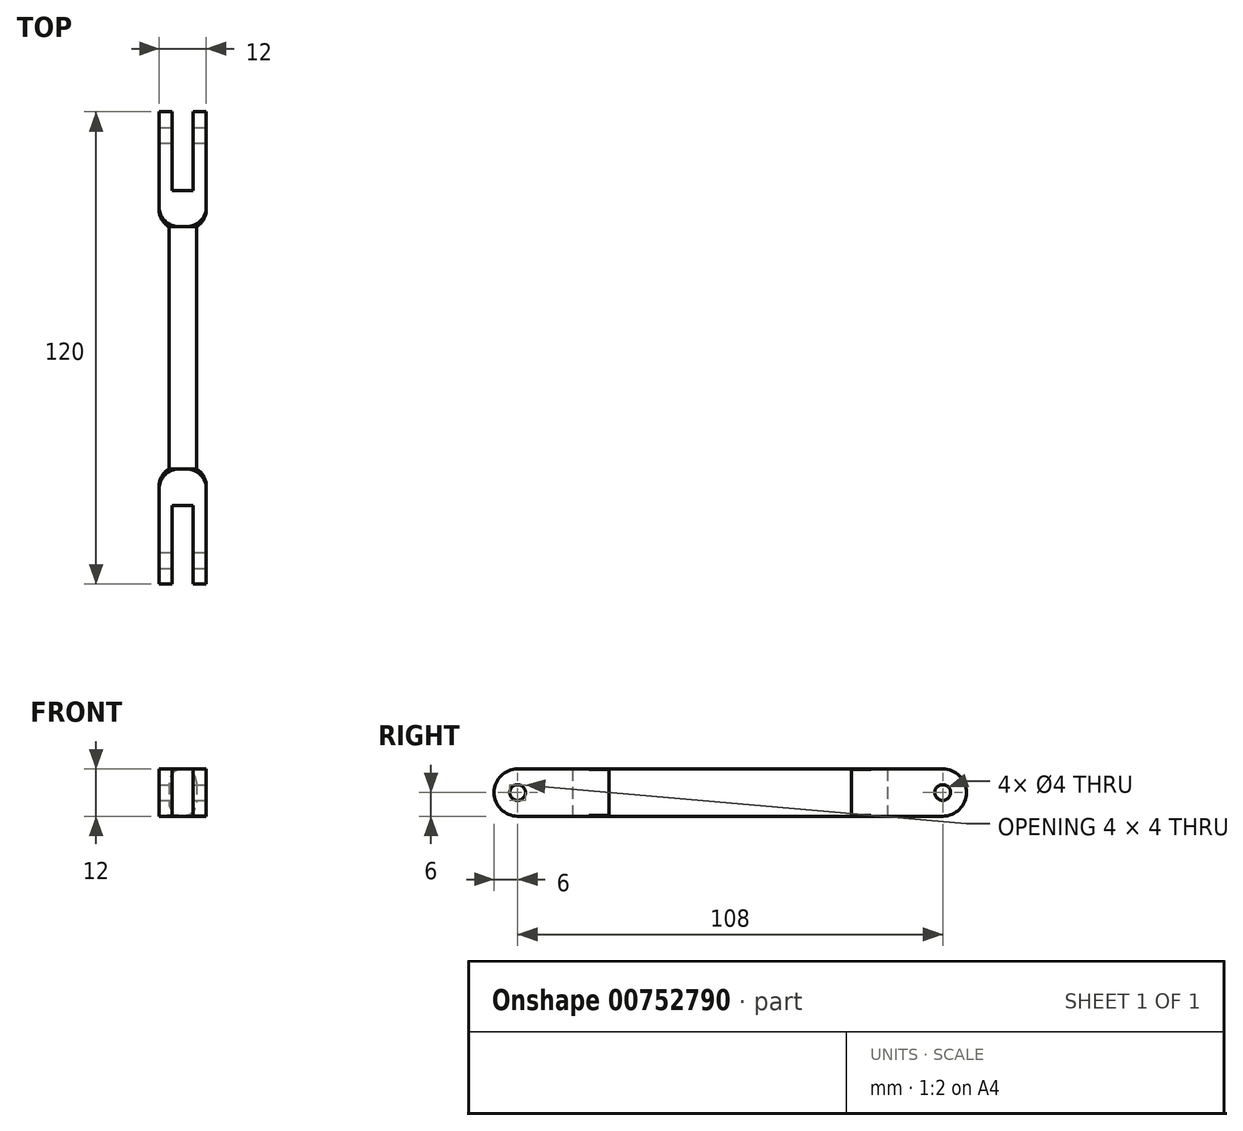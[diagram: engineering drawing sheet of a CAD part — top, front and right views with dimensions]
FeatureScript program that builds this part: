
annotation { "Feature Type Name" : "Feature", "Feature Type Description" : "" }
export const myFeature = defineFeature(function(context is Context, id is Id, definition is map)
    precondition{}
    {
        {
            var Q0;
            Q0=qCreatedBy(makeId("Top.planeOp"),FACE);
            var sketch = newSketch(context, id + "F0", { "sketchPlane" : qUnion([Q0])});
            skLineSegment(sketch, "E0.bottom", {"start": v(-6, -60) * mm, "end": v(6, -60) * mm});
            skLineSegment(sketch, "E0.top", {"start": v(-6, 60) * mm, "end": v(6, 60) * mm});
            skLineSegment(sketch, "E0.left", {"start": v(-6, -60) * mm, "end": v(-6, 60) * mm});
            skLineSegment(sketch, "E0.right", {"start": v(6, -60) * mm, "end": v(6, 60) * mm});
            skPoint(sketch, "E0.middle", {"position": v(0, 0) * mm});
            skLineSegment(sketch, "E1", {"start": v(0, -60) * mm, "end": v(0, -40) * mm, "construction": true});
            skLineSegment(sketch, "E2", {"start": v(0, -40) * mm, "end": v(2.65, -40) * mm});
            skLineSegment(sketch, "E3", {"start": v(2.65, -40) * mm, "end": v(2.65, -60) * mm});
            skLineSegment(sketch, "E4.MirrorCS", {"start": v(-2.65, -40) * mm, "end": v(-2.65, -60) * mm});
            skLineSegment(sketch, "E5.MirrorCS", {"start": v(0, -40) * mm, "end": v(-2.65, -40) * mm});
            skLineSegment(sketch, "E6", {"start": v(0, 0) * mm, "end": v(-2.66, 0) * mm, "construction": true});
            skLineSegment(sketch, "E7.MirrorCS", {"start": v(-2.65, 40) * mm, "end": v(-2.65, 60) * mm});
            skLineSegment(sketch, "E8.MirrorCS", {"start": v(2.65, 40) * mm, "end": v(2.65, 60) * mm});
            skLineSegment(sketch, "E9.MirrorCS", {"start": v(0, 40) * mm, "end": v(-2.65, 40) * mm});
            skLineSegment(sketch, "E10.MirrorCS", {"start": v(0, 40) * mm, "end": v(2.65, 40) * mm});
            skLineSegment(sketch, "E11.bottom", {"start": v(-3.5, -30.81) * mm, "end": v(3.5, -30.81) * mm});
            skLineSegment(sketch, "E11.top", {"start": v(-3.5, 30.81) * mm, "end": v(3.5, 30.81) * mm});
            skLineSegment(sketch, "E11.left", {"start": v(-3.5, -30.81) * mm, "end": v(-3.5, 30.81) * mm});
            skLineSegment(sketch, "E11.right", {"start": v(3.5, -30.81) * mm, "end": v(3.5, 30.81) * mm});
            skLineSegment(sketch, "E12", {"start": v(-3.5, -30.81) * mm, "end": v(-6, -30.81) * mm});
            skLineSegment(sketch, "E13", {"start": v(3.5, -30.81) * mm, "end": v(6, -30.81) * mm});
            skLineSegment(sketch, "E14", {"start": v(6, 30.81) * mm, "end": v(-6, 30.81) * mm});
            skSolve(sketch);
        }
        {
            var Q0;
            Q0=makeQuery(id+"F0.imprint","IMPRINT",FACE,{"disambiguationData":[TD([[makeQuery(id+"F0.imprint","IMPRINT",EDGE,{"derivedFrom":sQuery(id+"F0.wireOp",EDGE,"E11.bottom")}),1.0]])]});
            var Q1;
            {var subQ5=sQuery(id+"F0.wireOp",EDGE,"E7.MirrorCS");Q1=makeQuery(id+"F0.imprint","IMPRINT",FACE,{"disambiguationData":[TD([[makeQuery(id+"F0.imprint","IMPRINT",EDGE,{"derivedFrom":subQ5}),1.0]])]});}
            var Q2;
            Q2=makeQuery(id+"F0.imprint","IMPRINT",FACE,{"disambiguationData":[TD([[makeQuery(id+"F0.imprint","IMPRINT",EDGE,{"derivedFrom":sQuery(id+"F0.wireOp",EDGE,"E2")}),1.0]])]});
            extrude(context, id + "F1", {"entities" : qUnion([Q0, Q1, Q2]), "depth" : 12 * mm, "offsetDistance" : 25 * mm});
        }
        {
            var Q0;
            {var subQ0=sQuery(id+"F0.wireOp",EDGE,"E0.bottom");Q0=makeQuery(id+"F1.opExtrude","CAP_EDGE",EDGE,{"disambiguationData":[OSD([subQ0]),TDD([makeQuery(id+"F0.imprint","IMPRINT",EDGE,{"disambiguationData":[TD([[makeQuery(id+"F0.imprint","INTERSECT",VERTEX,{"derivedFrom":[subQ0,sQuery(id+"F0.wireOp",EDGE,"E0.right")]}),1.0]])],"derivedFrom":subQ0})])],"isStart":false});}
            var Q1;
            {var subQ0=sQuery(id+"F0.wireOp",EDGE,"E0.bottom");Q1=makeQuery(id+"F1.opExtrude","CAP_EDGE",EDGE,{"disambiguationData":[OSD([subQ0]),TDD([makeQuery(id+"F0.imprint","IMPRINT",EDGE,{"disambiguationData":[TD([[makeQuery(id+"F0.imprint","INTERSECT",VERTEX,{"derivedFrom":[subQ0,sQuery(id+"F0.wireOp",EDGE,"E0.right")]}),1.0]])],"derivedFrom":subQ0})])],"isStart":true});}
            var Q2;
            {var subQ0=sQuery(id+"F0.wireOp",EDGE,"E0.bottom");Q2=makeQuery(id+"F1.opExtrude","CAP_EDGE",EDGE,{"disambiguationData":[OSD([subQ0]),TDD([makeQuery(id+"F0.imprint","IMPRINT",EDGE,{"disambiguationData":[TD([[makeQuery(id+"F0.imprint","INTERSECT",VERTEX,{"derivedFrom":[subQ0,sQuery(id+"F0.wireOp",EDGE,"E4.MirrorCS")]}),1.0]])],"derivedFrom":subQ0})])],"isStart":false});}
            var Q3;
            {var subQ0=sQuery(id+"F0.wireOp",EDGE,"E0.bottom");Q3=makeQuery(id+"F1.opExtrude","CAP_EDGE",EDGE,{"disambiguationData":[OSD([subQ0]),TDD([makeQuery(id+"F0.imprint","IMPRINT",EDGE,{"disambiguationData":[TD([[makeQuery(id+"F0.imprint","INTERSECT",VERTEX,{"derivedFrom":[subQ0,sQuery(id+"F0.wireOp",EDGE,"E4.MirrorCS")]}),1.0]])],"derivedFrom":subQ0})])],"isStart":true});}
            var Q4;
            {var subQ0=sQuery(id+"F0.wireOp",EDGE,"E0.top");Q4=makeQuery(id+"F1.opExtrude","CAP_EDGE",EDGE,{"disambiguationData":[OSD([subQ0]),TDD([makeQuery(id+"F0.imprint","IMPRINT",EDGE,{"disambiguationData":[TD([[makeQuery(id+"F0.imprint","INTERSECT",VERTEX,{"derivedFrom":[subQ0,sQuery(id+"F0.wireOp",EDGE,"E0.right")]}),1.0]])],"derivedFrom":subQ0})])],"isStart":false});}
            var Q5;
            {var subQ0=sQuery(id+"F0.wireOp",EDGE,"E0.top");Q5=makeQuery(id+"F1.opExtrude","CAP_EDGE",EDGE,{"disambiguationData":[OSD([subQ0]),TDD([makeQuery(id+"F0.imprint","IMPRINT",EDGE,{"disambiguationData":[TD([[makeQuery(id+"F0.imprint","INTERSECT",VERTEX,{"derivedFrom":[subQ0,sQuery(id+"F0.wireOp",EDGE,"E7.MirrorCS")]}),1.0]])],"derivedFrom":subQ0})])],"isStart":false});}
            var Q6;
            {var subQ0=sQuery(id+"F0.wireOp",EDGE,"E0.top");Q6=makeQuery(id+"F1.opExtrude","CAP_EDGE",EDGE,{"disambiguationData":[OSD([subQ0]),TDD([makeQuery(id+"F0.imprint","IMPRINT",EDGE,{"disambiguationData":[TD([[makeQuery(id+"F0.imprint","INTERSECT",VERTEX,{"derivedFrom":[subQ0,sQuery(id+"F0.wireOp",EDGE,"E7.MirrorCS")]}),1.0]])],"derivedFrom":subQ0})])],"isStart":true});}
            var Q7;
            {var subQ0=sQuery(id+"F0.wireOp",EDGE,"E0.top");Q7=makeQuery(id+"F1.opExtrude","CAP_EDGE",EDGE,{"disambiguationData":[OSD([subQ0]),TDD([makeQuery(id+"F0.imprint","IMPRINT",EDGE,{"disambiguationData":[TD([[makeQuery(id+"F0.imprint","INTERSECT",VERTEX,{"derivedFrom":[subQ0,sQuery(id+"F0.wireOp",EDGE,"E0.right")]}),1.0]])],"derivedFrom":subQ0})])],"isStart":true});}
            fillet(context, id + "F2", {"entities" : qUnion([Q0, Q1, Q2, Q3, Q4, Q5, Q6, Q7]), "radius" : 6 * mm, "tangentPropagation" : true, "allowEdgeOverflow" : false});
        }
        {
            var Q0;
            Q0=makeQuery(id+"F1.opExtrude","CAP_EDGE",EDGE,{"disambiguationData":[OSD([sQuery(id+"F0.wireOp",EDGE,"E11.right")])],"isStart":false});
            var Q1;
            Q1=makeQuery(id+"F1.opExtrude","CAP_EDGE",EDGE,{"disambiguationData":[OSD([sQuery(id+"F0.wireOp",EDGE,"E11.left")])],"isStart":false});
            var Q2;
            Q2=makeQuery(id+"F1.opExtrude","CAP_EDGE",EDGE,{"disambiguationData":[OSD([sQuery(id+"F0.wireOp",EDGE,"E11.right")])],"isStart":true});
            var Q3;
            Q3=makeQuery(id+"F1.opExtrude","CAP_EDGE",EDGE,{"disambiguationData":[OSD([sQuery(id+"F0.wireOp",EDGE,"E11.left")])],"isStart":true});
            fillet(context, id + "F3", {"entities" : qUnion([Q0, Q1, Q2, Q3]), "radius" : 3.5 * mm, "tangentPropagation" : true, "allowEdgeOverflow" : false});
        }
        {
            var Q0;
            Q0=makeQuery(id+"F1.opExtrude","SWEPT_EDGE",EDGE,{"disambiguationData":[OSD([sQuery(id+"F0.wireOp",EDGE,"E0.left"),sQuery(id+"F0.wireOp",EDGE,"E14")])]});
            var Q1;
            Q1=makeQuery(id+"F1.opExtrude","SWEPT_EDGE",EDGE,{"disambiguationData":[OSD([sQuery(id+"F0.wireOp",EDGE,"E0.left"),sQuery(id+"F0.wireOp",EDGE,"E12")])]});
            var Q2;
            Q2=makeQuery(id+"F1.opExtrude","SWEPT_EDGE",EDGE,{"disambiguationData":[OSD([sQuery(id+"F0.wireOp",EDGE,"E0.right"),sQuery(id+"F0.wireOp",EDGE,"E14")])]});
            var Q3;
            Q3=makeQuery(id+"F1.opExtrude","SWEPT_EDGE",EDGE,{"disambiguationData":[OSD([sQuery(id+"F0.wireOp",EDGE,"E0.right"),sQuery(id+"F0.wireOp",EDGE,"E13")])]});
            fillet(context, id + "F4", {"entities" : qUnion([Q0, Q1, Q2, Q3]), "radius" : 5 * mm, "tangentPropagation" : true, "allowEdgeOverflow" : false});
        }
        {
            var Q0;
            Q0=qCreatedBy(makeId("Right.planeOp"),FACE);
            var sketch = newSketch(context, id + "F5", { "sketchPlane" : qUnion([Q0])});
            skLineSegment(sketch, "E15", {"start": v(0, 0) * mm, "end": v(0, 6) * mm, "construction": true});
            skLineSegment(sketch, "E16", {"start": v(0, 6) * mm, "end": v(54, 6) * mm, "construction": true});
            skCircle(sketch, "E17", {"center": v(54, 6) * mm, "radius": 2 * mm});
            skCircle(sketch, "E18.MirrorC", {"center": v(-54, 6) * mm, "radius": 2 * mm});
            skSolve(sketch);
        }
        {
            var Q0;
            Q0=qSketchRegion(id+"F5",true);
            extrude(context, id + "F6", {"entities" : qUnion([Q0]), "operationType" : NewBodyOperationType.REMOVE, "endBound" : BoundingType.SYMMETRIC, "oppositeDirection" : true, "depth" : 25 * mm, "offsetDistance" : 25 * mm});
        }
    });
